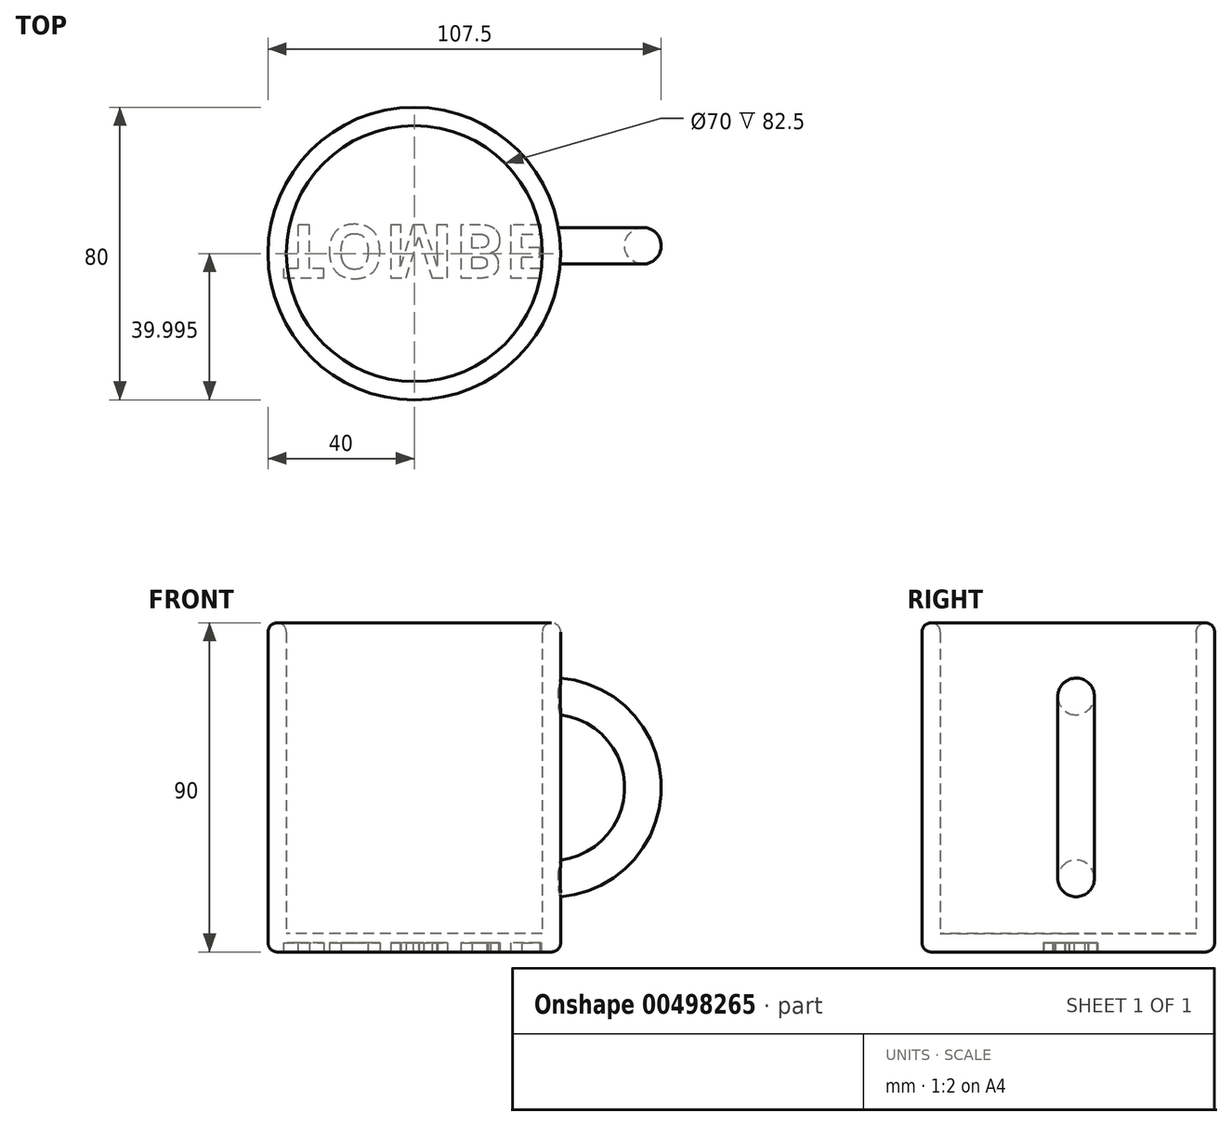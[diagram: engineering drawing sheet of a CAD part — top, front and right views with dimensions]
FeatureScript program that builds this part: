
annotation { "Feature Type Name" : "Feature", "Feature Type Description" : "" }
export const myFeature = defineFeature(function(context is Context, id is Id, definition is map)
    precondition{}
    {
        {
            var Q0;
            Q0=qCreatedBy(makeId("Top.planeOp"),FACE);
            var sketch = newSketch(context, id + "F0", { "sketchPlane" : qUnion([Q0])});
            skCircle(sketch, "E0", {"center": v(0, -2.13) * mm, "radius": 40 * mm});
            skSolve(sketch);
        }
        {
            var Q0;
            Q0=makeQuery(id+"F0.imprint","IMPRINT",FACE,{"disambiguationData":[TD([[makeQuery(id+"F0.imprint","IMPRINT",EDGE,{"derivedFrom":sQuery(id+"F0.wireOp",EDGE,"E0")}),1.0]])]});
            var Q1;
            Q1=sQuery(id+"F0.wireOp",EDGE,"E0");
            extrude(context, id + "F1", {"entities" : qUnion([Q0]), "surfaceEntities" : qUnion([Q1]), "depth" : 90 * mm});
        }
        {
            var Q0;
            Q0=makeQuery(id+"F1.opExtrude","CAP_FACE",FACE,{"disambiguationData":[OSD([sQuery(id+"F0.wireOp",EDGE,"E0")])],"isStart":false});
            shell(context, id + "F2", {"entities" : qUnion([Q0]), "thickness" : 5 * mm});
        }
        {
            var Q0;
            Q0=qCreatedBy(makeId("Right.planeOp"),FACE);
            cPlane(context, id + "F3", {"entities" : qUnion([Q0]), "cplaneType" : CPlaneType.OFFSET, "offset" : 37.5 * mm, "width" : 150 * mm, "height" : 150 * mm});
        }
        {
            var Q0;
            Q0=qCreatedBy(id+"F3.planeOp",FACE);
            var sketch = newSketch(context, id + "F4", { "sketchPlane" : qUnion([Q0])});
            skCircle(sketch, "E1", {"center": v(0, 70) * mm, "radius": 5 * mm});
            skLineSegment(sketch, "E2", {"start": v(0, 45) * mm, "end": v(24.47, 45) * mm});
            skSolve(sketch);
        }
        {
            var Q0;
            Q0 = qSketchRegion(id + "F4", true);
            var Q1;
            Q1=sQuery(id+"F4.wireOp",EDGE,"E2");
            revolve(context, id + "F5", {"operationType" : NewBodyOperationType.ADD, "entities" : qUnion([Q0]), "axis" : qUnion([Q1]), "revolveType" : RevolveType.ONE_DIRECTION, "angle" : 180 * degree});
        }
        {
            var Q0;
            Q0=makeQuery(id+"F1.opExtrude","CAP_EDGE",EDGE,{"disambiguationData":[OSD([sQuery(id+"F0.wireOp",EDGE,"E0")])],"isStart":false});
            var Q1;
            {var subQ0=sQuery(id+"F0.wireOp",EDGE,"E0");Q1=makeQuery(id+"F2.opShell","OFFSET_EDGE",EDGE,{"disambiguationData":[OSD([subQ0]),TDD([makeQuery(id+"F1.opExtrude","CAP_EDGE",EDGE,{"disambiguationData":[OSD([subQ0])],"isStart":false})])]});}
            var Q2;
            Q2=makeQuery(id+"F1.opExtrude","CAP_EDGE",EDGE,{"disambiguationData":[OSD([sQuery(id+"F0.wireOp",EDGE,"E0")])],"isStart":true});
            fillet(context, id + "F6", {"entities" : qUnion([Q0, Q1, Q2]), "radius" : 2.5 * mm, "tangentPropagation" : true, "allowEdgeOverflow" : false});
        }
        {
            var Q0;
            Q0=makeQuery(id+"F1.opExtrude","CAP_FACE",FACE,{"disambiguationData":[OSD([sQuery(id+"F0.wireOp",EDGE,"E0")])],"isStart":true});
            var sketch = newSketch(context, id + "F7", { "sketchPlane" : qUnion([Q0])});
            skText(sketch, "E3", { "text": "TOMBE", "fontName": "OpenSans-Bold.ttf"});
            const initialGuessF7  = {"E3": [-0.03614, -0.0057, 1, 0, 0.0146]};
            skSetInitialGuess(sketch, initialGuessF7);
            skSolve(sketch);
        }
        {
            var Q0;
            Q0 = qSketchRegion(id + "F7", true);
            extrude(context, id + "F8", {"entities" : qUnion([Q0]), "operationType" : NewBodyOperationType.REMOVE, "oppositeDirection" : true, "depth" : 2.5 * mm});
        }
    });
